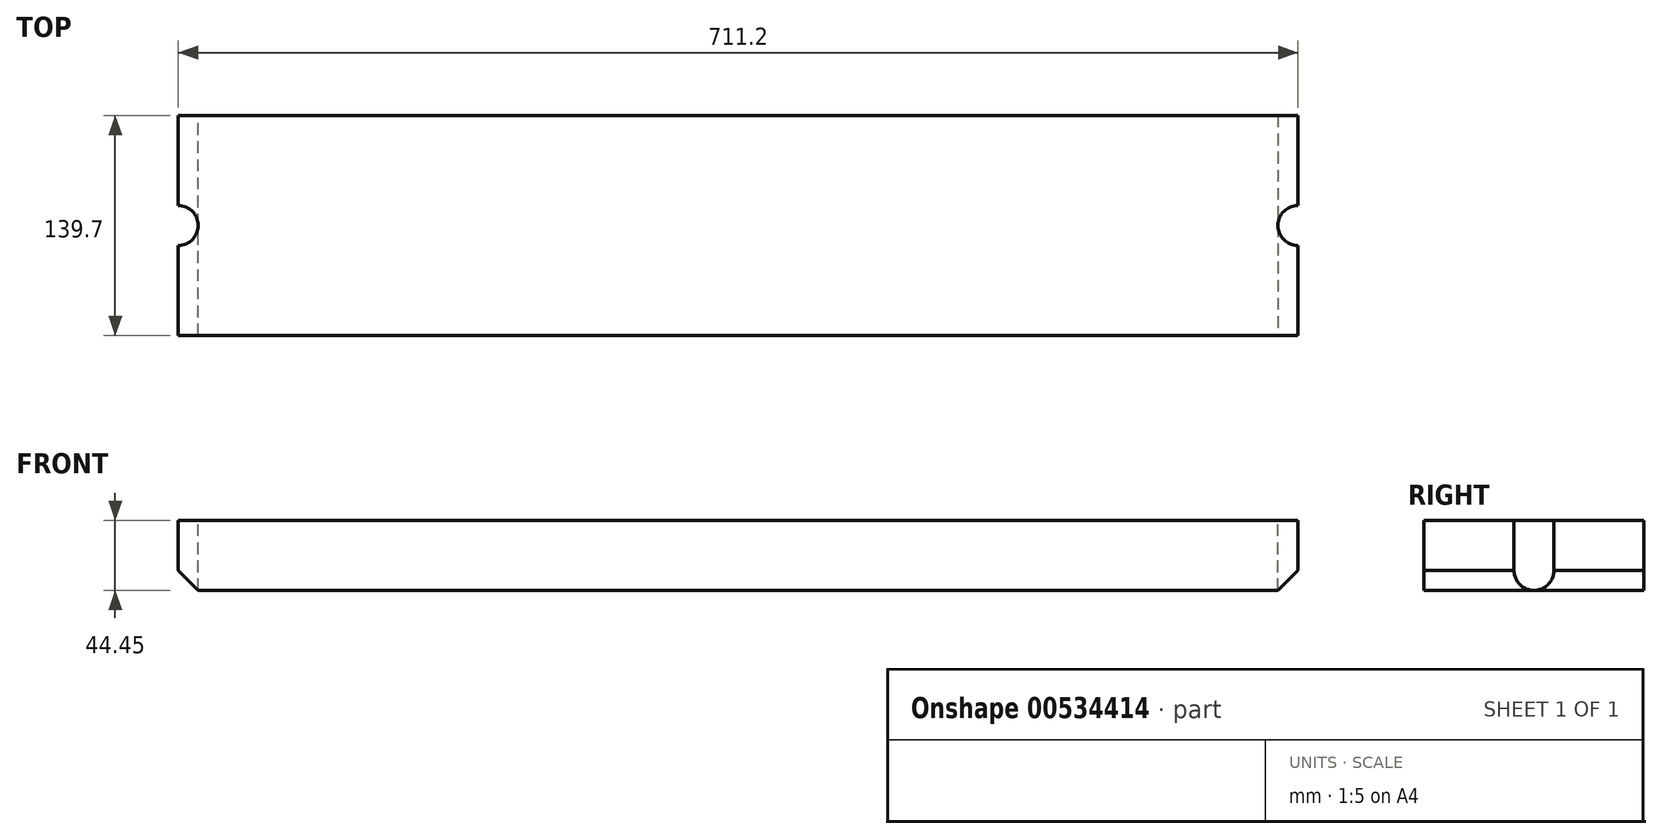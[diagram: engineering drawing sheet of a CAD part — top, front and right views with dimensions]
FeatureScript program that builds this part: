
annotation { "Feature Type Name" : "Feature", "Feature Type Description" : "" }
export const myFeature = defineFeature(function(context is Context, id is Id, definition is map)
    precondition{}
    {
        {
            var Q0;
            Q0=qCreatedBy(makeId("Top.planeOp"),FACE);
            var sketch = newSketch(context, id + "F0", { "sketchPlane" : qUnion([Q0])});
            skLineSegment(sketch, "E0.bottom", {"start": v(0, 0) * mm, "end": v(711.2, 0) * mm});
            skLineSegment(sketch, "E0.top", {"start": v(0, 139.7) * mm, "end": v(711.2, 139.7) * mm});
            skLineSegment(sketch, "E0.left", {"start": v(0, 0) * mm, "end": v(0, 139.7) * mm});
            skLineSegment(sketch, "E0.right", {"start": v(711.2, 0) * mm, "end": v(711.2, 139.7) * mm});
            skSolve(sketch);
        }
        {
            var Q0;
            Q0 = qSketchRegion(id + "F0", true);
            extrude(context, id + "F1", {"entities" : qUnion([Q0]), "depth" : 44.45 * mm, "offsetDistance" : 25.4 * mm});
        }
        {
            var Q0;
            Q0=makeQuery(id+"F1.opExtrude","CAP_EDGE",EDGE,{"disambiguationData":[OSD([sQuery(id+"F0.wireOp",EDGE,"E0.left")])],"isStart":true});
            var Q1;
            Q1=makeQuery(id+"F1.opExtrude","CAP_EDGE",EDGE,{"disambiguationData":[OSD([sQuery(id+"F0.wireOp",EDGE,"E0.right")])],"isStart":true});
            chamfer(context, id + "F2", {"entities" : qUnion([Q0, Q1]), "width" : 12.7 * mm, "tangentPropagation" : true});
        }
        {
            var Q0;
            Q0=makeQuery(id+"F1.opExtrude","CAP_FACE",FACE,{"disambiguationData":[OSD([sQuery(id+"F0.wireOp",EDGE,"E0.bottom"),sQuery(id+"F0.wireOp",EDGE,"E0.top"),sQuery(id+"F0.wireOp",EDGE,"E0.left"),sQuery(id+"F0.wireOp",EDGE,"E0.right")])],"isStart":false});
            var sketch = newSketch(context, id + "F3", { "sketchPlane" : qUnion([Q0])});
            skLineSegment(sketch, "E1", {"start": v(355.6, 153.84) * mm, "end": v(355.6, -32.66) * mm, "construction": true});
            skPoint(sketch, "E1.startSnap0", {"position": v(355.6, 139.7) * mm});
            skLineSegment(sketch, "E2", {"start": v(-32.44, 69.85) * mm, "end": v(724.16, 69.85) * mm, "construction": true});
            skPoint(sketch, "E2.startSnap0", {"position": v(0, 69.85) * mm});
            skArc(sketch, "E3", {"start": v(0, 57.15) * mm, "mid": v(12.7, 69.85) * mm, "end": v(0, 82.55) * mm});
            skLineSegment(sketch, "E4", {"start": v(0, 82.55) * mm, "end": v(0, 57.15) * mm});
            skArc(sketch, "E5.MirrorCS", {"start": v(711.2, 57.15) * mm, "mid": v(698.5, 69.85) * mm, "end": v(711.2, 82.55) * mm});
            skLineSegment(sketch, "E6.MirrorCS", {"start": v(711.2, 82.55) * mm, "end": v(711.2, 57.15) * mm});
            skSolve(sketch);
        }
        {
            var Q0;
            Q0 = qSketchRegion(id + "F3", true);
            extrude(context, id + "F4", {"entities" : qUnion([Q0]), "operationType" : NewBodyOperationType.REMOVE, "oppositeDirection" : true, "depth" : 44.45 * mm, "offsetDistance" : 25.4 * mm});
        }
    });
